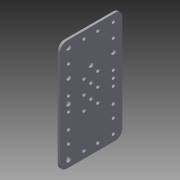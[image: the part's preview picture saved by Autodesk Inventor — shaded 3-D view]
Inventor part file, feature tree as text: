
AUTODESK INVENTOR PART (.ipt)
format: ipt  version: 2013 (Build 170138000, 138)  size: 145,920 bytes
history: native  units: in
note: dims shown in document units (in); Inventor stores cm internally (conversion verified against a paired STEP export)
features: other x1, imported_body x1, sketch x1
ambient origin geometry x8: Origin, YZ Plane, XZ Plane, XY Plane, X Axis, Y Axis, Z Axis, Center Point
feature tree (3):
  other  "C14005"
  imported_body  "Base1"
  sketch  "Sketch1"
